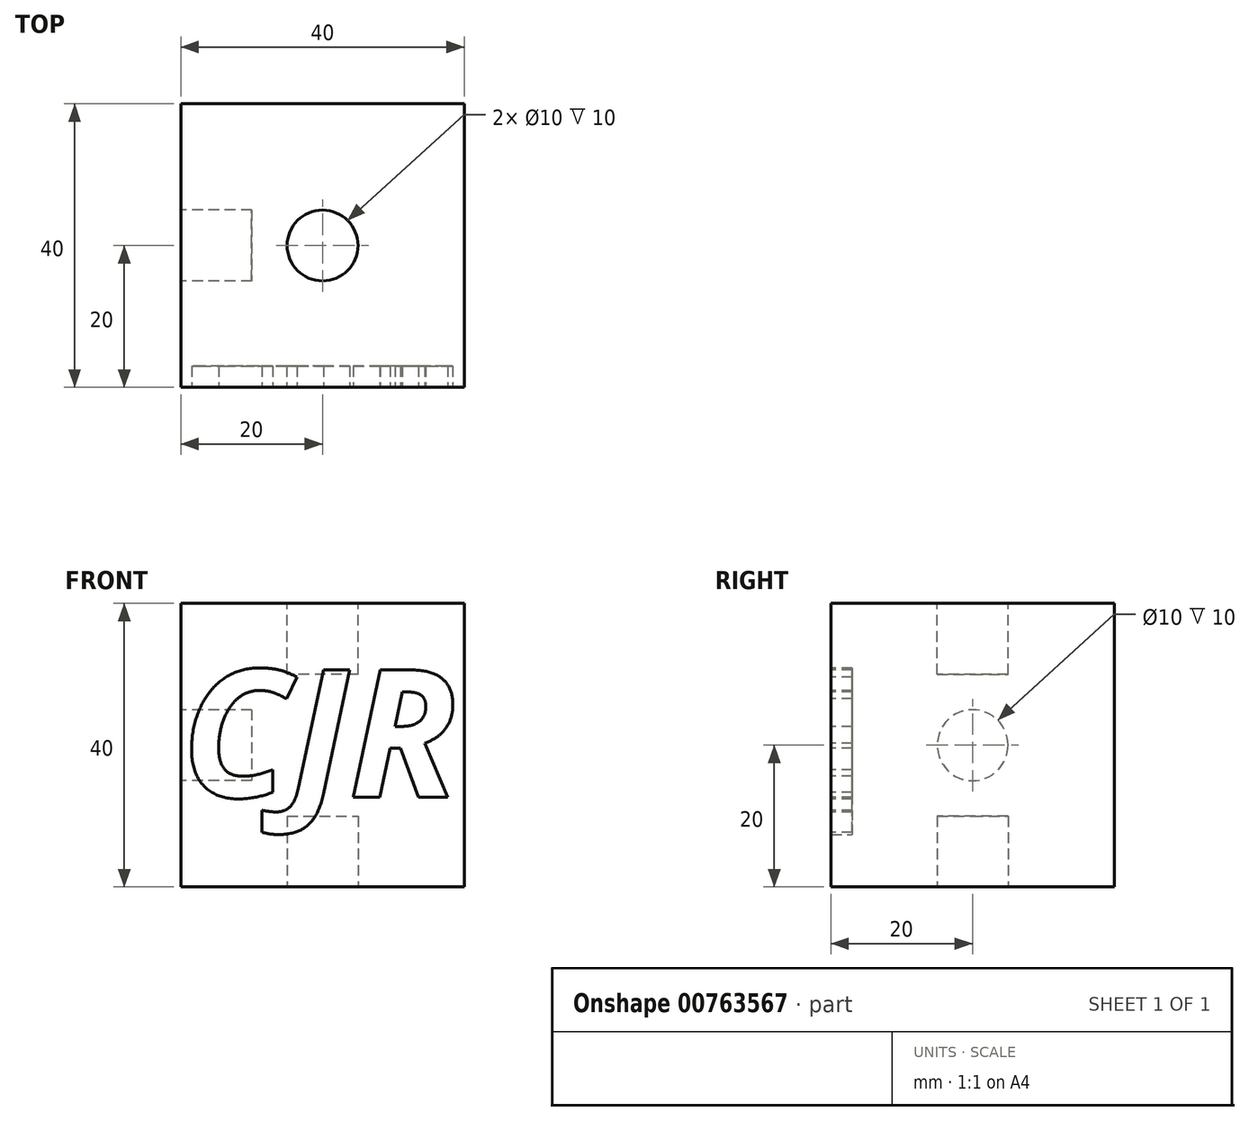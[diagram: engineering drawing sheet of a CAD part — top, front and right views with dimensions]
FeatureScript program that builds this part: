
annotation { "Feature Type Name" : "Feature", "Feature Type Description" : "" }
export const myFeature = defineFeature(function(context is Context, id is Id, definition is map)
    precondition{}
    {
        {
            var Q0;
            Q0=qCreatedBy(makeId("Front.planeOp"),FACE);
            var sketch = newSketch(context, id + "F0", { "sketchPlane" : qUnion([Q0])});
            skLineSegment(sketch, "E0.bottom", {"start": v(-20, 20) * mm, "end": v(20, 20) * mm});
            skLineSegment(sketch, "E0.top", {"start": v(-20, -20) * mm, "end": v(20, -20) * mm});
            skLineSegment(sketch, "E0.left", {"start": v(-20, 20) * mm, "end": v(-20, -20) * mm});
            skLineSegment(sketch, "E0.right", {"start": v(20, 20) * mm, "end": v(20, -20) * mm});
            skSolve(sketch);
        }
        {
            var Q0;
            Q0 = qSketchRegion(id + "F0", true);
            extrude(context, id + "F1", {"entities" : qUnion([Q0]), "endBound" : BoundingType.SYMMETRIC, "depth" : 40 * mm, "offsetDistance" : 25 * mm});
        }
        {
            var Q0;
            Q0=makeQuery(id+"F1.opExtrude","CAP_FACE",FACE,{"disambiguationData":[OSD([sQuery(id+"F0.wireOp",EDGE,"E0.bottom"),sQuery(id+"F0.wireOp",EDGE,"E0.top"),sQuery(id+"F0.wireOp",EDGE,"E0.left"),sQuery(id+"F0.wireOp",EDGE,"E0.right")])],"isStart":false});
            var sketch = newSketch(context, id + "F2", { "sketchPlane" : qUnion([Q0])});
            skText(sketch, "E1", { "text": "CJR", "fontName": "OpenSans-BoldItalic.ttf"});
            const initialGuessF2  = {"E1": [-0.02, -0.00733, 1, 0, 0.0181]};
            skSetInitialGuess(sketch, initialGuessF2);
            skSolve(sketch);
        }
        {
            var Q0;
            Q0 = qSketchRegion(id + "F2", true);
            extrude(context, id + "F3", {"entities" : qUnion([Q0]), "operationType" : NewBodyOperationType.REMOVE, "oppositeDirection" : true, "depth" : 3 * mm, "offsetDistance" : 25 * mm});
        }
        {
            var Q0;
            Q0=makeQuery(id+"F1.opExtrude","SWEPT_FACE",FACE,{"disambiguationData":[OSD([sQuery(id+"F0.wireOp",EDGE,"E0.left")])]});
            var sketch = newSketch(context, id + "F4", { "sketchPlane" : qUnion([Q0])});
            skCircle(sketch, "E2", {"center": v(0, 0) * mm, "radius": 5 * mm});
            skSolve(sketch);
        }
        {
            var Q0;
            Q0 = qSketchRegion(id + "F4", true);
            extrude(context, id + "F5", {"entities" : qUnion([Q0]), "operationType" : NewBodyOperationType.REMOVE, "oppositeDirection" : true, "depth" : 10 * mm, "offsetDistance" : 25 * mm});
        }
        {
            var Q0;
            Q0=makeQuery(id+"F1.opExtrude","SWEPT_FACE",FACE,{"disambiguationData":[OSD([sQuery(id+"F0.wireOp",EDGE,"E0.top")])]});
            var sketch = newSketch(context, id + "F6", { "sketchPlane" : qUnion([Q0])});
            skCircle(sketch, "E3", {"center": v(0, 0) * mm, "radius": 5 * mm});
            skSolve(sketch);
        }
        {
            var Q0;
            Q0 = qSketchRegion(id + "F6", true);
            extrude(context, id + "F7", {"entities" : qUnion([Q0]), "operationType" : NewBodyOperationType.REMOVE, "oppositeDirection" : true, "depth" : 10 * mm, "offsetDistance" : 25 * mm});
        }
        {
            var Q0;
            Q0=makeQuery(id+"F1.opExtrude","SWEPT_FACE",FACE,{"disambiguationData":[OSD([sQuery(id+"F0.wireOp",EDGE,"E0.bottom")])]});
            var sketch = newSketch(context, id + "F8", { "sketchPlane" : qUnion([Q0])});
            skCircle(sketch, "E4", {"center": v(0, 0) * mm, "radius": 5 * mm});
            skSolve(sketch);
        }
        {
            var Q0;
            Q0 = qSketchRegion(id + "F8", true);
            extrude(context, id + "F9", {"entities" : qUnion([Q0]), "operationType" : NewBodyOperationType.REMOVE, "oppositeDirection" : true, "depth" : 10 * mm, "offsetDistance" : 25 * mm});
        }
    });
